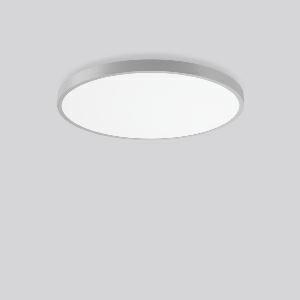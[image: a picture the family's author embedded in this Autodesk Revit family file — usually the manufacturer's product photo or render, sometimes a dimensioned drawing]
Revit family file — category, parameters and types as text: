
# Revit family: triona_round_a_312388_004_1_76_c962
name_source: partatom
category: Lighting Fixtures
units: mm (PartAtom-declared; Revit-internal decimal feet)

## family parameters
Cut with Voids When Loaded = No
Host = Face
Light Source = No
Part Type = Normal
Room Calculation Point = No
Round Connector Dimension = Use Diameter
Shared = No

## types (1)
- TRIONA round A (1 x LED Modul 840, 12900 lm, 4000)
    Apparent Load = 133 VA
    CIE Flux Codes = 49 80 96 71 100
    Color Rendering = 80
    Color Temperature = 4000
    Default Elevation = 1800 mm
    Description = Series: TRIONA round
Decorative round LED surface-mounted luminaire. Flat, seamless frame: aluminium extrusion profile, powder coated. Cover made of sheet steel, powder-coated. Direct light emission through a diffuser plastic opal. Indirect light emission through a flush diffuser made of satin-finish plastic. Lightguide and diffuser made of non-yellowing plastic (PMMA). Lateral light emission (RZB SIDELITE technology) for above-average homogeneous light distribution. Direct 70%, indirect 30% light emission. Suitable for Ceiling mounting, Wall (surface). Tool-free mounting via bayonet connection. Electronic ballast included. Very easy installation thanks to Plug+Play connection. 
Colour: silver, matt (approx. RAL 9006)
Diameter: 845 mm
Height: 88 mm
Lamp: LED
Socket: without socket
Colour temperature: 4000K
Colour rendering index (CRI): 80
System power: 133 W
Rated luminous flux: 12900 lm
Luminous efficiency: 97 lm/W
Control gear: Converter, dimmable, DALI
Protection class: I
Type of protection: IP 20
    Height = 88 mm
    Lamp = 1 x LED Modul 840
    Lamp Light Flux = 12900 lm
    Lamp count = 1
    Length = 845 mm
    Lifetime = 50000 h
    Luminous efficacy = 97 lm/W
    Manufacturer = RZB
    ModVariant = No
    Model = 312388.004.1.76
    Mounting Place = Ceiling
    Mounting Type = Surface mounted
    Number of Poles = 1
    OnlyDefault = Yes
    Power Factor = 1
    Product Name = TRIONA round A
    Product group = Surface mounted modular luminaires
    ProductGroupID = 306
    Protection Class = Protection class I
    Protection Degree = IP 20
    RLX_Detail_Level = 1
    RLX_Emergency_Light_Flux = 0 lm
    RLX_Emergency_Type = 0
    RLX_Emergency_Type_DB = No
    RlxData = <blob elided: 41817 chars, md5=7d98094a>
    Socket = socket
    Standby Power = 0 W
    System Light Flux = 12900 lm
    System Power = 133 W
    Type Comments = Product without accessories
    Type Image = 312388.004.jpg
    URL = http://relux.com
    VarID = ---
    Voltage = 230 V
    Voltage Range = 220-240 V
    Weight = 0.00 kg
    Width = 0 mm  [stored 0 ft]

note: [stored X ft] marks values corroborated as IEEE doubles in the binary element streams (Revit-internal decimal feet)

## geometry (parser evidence)
native form markers: Blend x4, Sweep x15
no freeform markers — native parametric forms only
